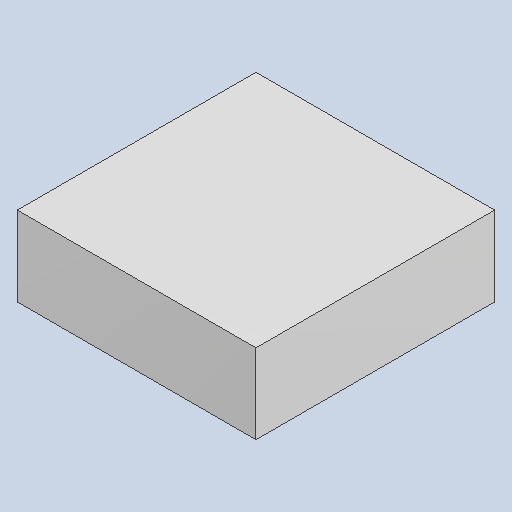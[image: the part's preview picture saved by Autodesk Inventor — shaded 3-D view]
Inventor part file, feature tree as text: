
AUTODESK INVENTOR PART (.ipt)
format: ipt  version: 2023.4 (Build 274418000, 418)  size: 79,872 bytes
history: native  units: mm
features: extrude x1
ambient origin geometry x8: Origin, YZ Plane, XZ Plane, XY Plane, X Axis, Y Axis, Z Axis, Center Point
bodies: Solid1 (feature_tree)
feature tree (1):
  extrude  "Extruded_7"  [1 undecoded]
note: 1 required parameter value undecoded (feature->parameter linkage not recoverable at this tier; creation-order binding heuristic only, values carry confidence <= 0.55)
